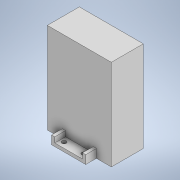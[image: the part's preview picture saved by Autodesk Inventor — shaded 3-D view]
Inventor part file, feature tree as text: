
AUTODESK INVENTOR PART (.ipt)
format: ipt  version: 2021.4 (Build 254397000, 397)  size: 131,072 bytes
history: native  units: mm
features: sketch x4, extrude x3, other x1, hole x1
ambient origin geometry x8: Origin, YZ Plane, XZ Plane, XY Plane, X Axis, Y Axis, Z Axis, Center Point
bodies: Body1 (feature_tree)
feature tree (9):
  other  "ソリッド1"
  extrude  "押し出し1"  Depth=60.0mm
  extrude  "押し出し2"  Depth=30.0mm
  extrude  "押し出し3"  Depth=85.0mm TaperAngle=0.0deg
  hole  "穴1"  [1 undecoded]
  sketch  "スケッチ1"
  sketch  "スケッチ2"
  sketch  "スケッチ3"
  sketch  "スケッチ4"
note: 1 required parameter value undecoded (feature->parameter linkage not recoverable at this tier; creation-order binding heuristic only, values carry confidence <= 0.55)
